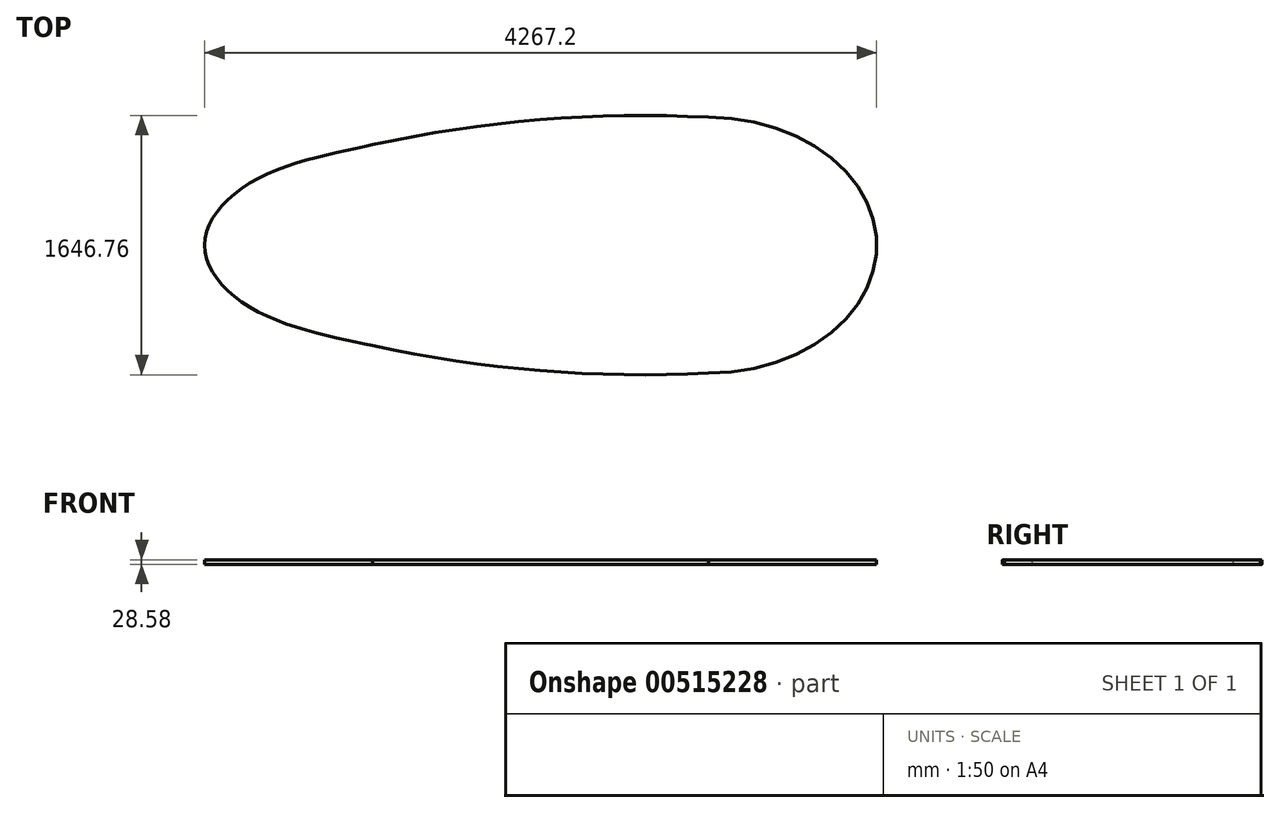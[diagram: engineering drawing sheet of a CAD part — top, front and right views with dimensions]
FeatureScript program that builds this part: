
annotation { "Feature Type Name" : "Feature", "Feature Type Description" : "" }
export const myFeature = defineFeature(function(context is Context, id is Id, definition is map)
    precondition{}
    {
        {
            var Q0;
            Q0=qCreatedBy(makeId("Top.planeOp"),FACE);
            var sketch = newSketch(context, id + "F0", { "sketchPlane" : qUnion([Q0])});
            skPoint(sketch, "E0.middle", {"position": v(0, 0) * mm});
            skLineSegment(sketch, "E1", {"start": v(2042.28, 0) * mm, "end": v(975.48, 0) * mm});
            skLineSegment(sketch, "E2", {"start": v(975.48, 0) * mm, "end": v(0, 0) * mm});
            skLineSegment(sketch, "E3", {"start": v(975.48, 0) * mm, "end": v(-91.32, 0) * mm});
            skLineSegment(sketch, "E4", {"start": v(-91.32, 0) * mm, "end": v(-1158.12, 0) * mm});
            skLineSegment(sketch, "E5", {"start": v(-1158.12, 0) * mm, "end": v(-2224.92, 0) * mm});
            skLineSegment(sketch, "E6", {"start": v(975.48, 0) * mm, "end": v(975.48, 812.8) * mm});
            skLineSegment(sketch, "E7", {"start": v(975.48, 0) * mm, "end": v(975.48, -812.8) * mm});
            skLineSegment(sketch, "E8", {"start": v(-91.32, 0) * mm, "end": v(-91.32, 796.93) * mm});
            skLineSegment(sketch, "E9", {"start": v(-91.32, 0) * mm, "end": v(-91.32, -796.92) * mm});
            skLineSegment(sketch, "E10", {"start": v(-1158.12, 0) * mm, "end": v(-1158.12, 638.18) * mm});
            skLineSegment(sketch, "E11", {"start": v(-1158.12, 0) * mm, "end": v(-1158.12, -638.17) * mm});
            skArc(sketch, "E12", {"start": v(975.48, 812.8) * mm, "mid": v(-97.13, 796.45) * mm, "end": v(-1158.12, 638.17) * mm});
            skArc(sketch, "E13", {"start": v(-1158.12, -638.17) * mm, "mid": v(-97.13, -796.45) * mm, "end": v(975.48, -812.8) * mm});
            skEllipse(sketch, "E14", {"center": v(975.48, 0) * mm, "majorRadius": 812.8 * mm, "minorRadius": 1066.8 * mm, "majorAxis": v(0, 1)});
            skLineSegment(sketch, "E15", {"start": v(-2224.92, 0) * mm, "end": v(-1691.52, 0) * mm});
            skFitSpline(sketch, "E16", {"points": [v(-1158.12, 638.18) * mm, v(-1939.17, 393.7) * mm, v(-2224.92, 0) * mm, v(-1939.17, -393.7) * mm, v(-1158.12, -638.17) * mm], "startDerivative": vector(-2374.22, -488.27) * mm, "endDerivative": vector(2374.22, -488.27) * mm});
            skSolve(sketch);
        }
        {
            var Q0;
            Q0=makeQuery(id+"F0.imprint","IMPRINT",FACE,{"disambiguationData":[TD([[makeQuery(id+"F0.imprint","IMPRINT",EDGE,{"derivedFrom":sQuery(id+"F0.wireOp",EDGE,"E4")}),-1.0]])]});
            var Q1;
            Q1=makeQuery(id+"F0.imprint","IMPRINT",FACE,{"disambiguationData":[TD([[makeQuery(id+"F0.imprint","IMPRINT",EDGE,{"derivedFrom":sQuery(id+"F0.wireOp",EDGE,"E5")}),-1.0]])]});
            var Q2;
            Q2=makeQuery(id+"F0.imprint","IMPRINT",FACE,{"disambiguationData":[TD([[makeQuery(id+"F0.imprint","IMPRINT",EDGE,{"derivedFrom":sQuery(id+"F0.wireOp",EDGE,"E5")}),1.0]])]});
            var Q3;
            Q3=makeQuery(id+"F0.imprint","IMPRINT",FACE,{"disambiguationData":[TD([[makeQuery(id+"F0.imprint","IMPRINT",EDGE,{"derivedFrom":sQuery(id+"F0.wireOp",EDGE,"E4")}),1.0]])]});
            var Q4;
            {var subQ0=sQuery(id+"F0.wireOp",EDGE,"E7");Q4=makeQuery(id+"F0.imprint","IMPRINT",FACE,{"disambiguationData":[TD([[makeQuery(id+"F0.imprint","IMPRINT",EDGE,{"derivedFrom":subQ0}),-1.0]])]});}
            var Q5;
            {var subQ0=sQuery(id+"F0.wireOp",EDGE,"E9");Q5=makeQuery(id+"F0.imprint","IMPRINT",FACE,{"disambiguationData":[TD([[makeQuery(id+"F0.imprint","IMPRINT",EDGE,{"derivedFrom":subQ0}),1.0]])]});}
            var Q6;
            {var subQ0=sQuery(id+"F0.wireOp",EDGE,"E6");Q6=makeQuery(id+"F0.imprint","IMPRINT",FACE,{"disambiguationData":[TD([[makeQuery(id+"F0.imprint","IMPRINT",EDGE,{"derivedFrom":subQ0}),1.0]])]});}
            var Q7;
            {var subQ0=sQuery(id+"F0.wireOp",EDGE,"E8");Q7=makeQuery(id+"F0.imprint","IMPRINT",FACE,{"disambiguationData":[TD([[makeQuery(id+"F0.imprint","IMPRINT",EDGE,{"derivedFrom":subQ0}),-1.0]])]});}
            var Q8;
            {var subQ0=sQuery(id+"F0.wireOp",EDGE,"E1");Q8=makeQuery(id+"F0.imprint","IMPRINT",FACE,{"disambiguationData":[TD([[makeQuery(id+"F0.imprint","IMPRINT",EDGE,{"derivedFrom":subQ0}),-1.0]])]});}
            var Q9;
            {var subQ0=sQuery(id+"F0.wireOp",EDGE,"E1");Q9=makeQuery(id+"F0.imprint","IMPRINT",FACE,{"disambiguationData":[TD([[makeQuery(id+"F0.imprint","IMPRINT",EDGE,{"derivedFrom":subQ0}),1.0]])]});}
            extrude(context, id + "F1", {"entities" : qUnion([Q0, Q1, Q2, Q3, Q4, Q5, Q6, Q7, Q8, Q9]), "depth" : 28.57 * mm});
        }
    });
